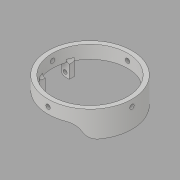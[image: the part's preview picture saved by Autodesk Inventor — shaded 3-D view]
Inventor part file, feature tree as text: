
AUTODESK INVENTOR PART (.ipt)
format: ipt  version: 2017 (Build 210142000, 142)  size: 249,856 bytes
history: native  units: in
note: dims shown in document units (in); Inventor stores cm internally (conversion verified against a paired STEP export)
features: sketch x6, extrude x5, fillet x3, hole x1
ambient origin geometry x8: Origin, YZ Plane, XZ Plane, XY Plane, X Axis, Y Axis, Z Axis, Center Point
bodies: Solid1 (feature_tree)
feature tree (15):
  extrude  "Extrusion1"  Depth=0.2in
  extrude  "Extrusion2"  Depth=1.5in
  hole  "Hole2"  [1 undecoded]
  fillet  "Fillet1"  Radius=0.6in
  extrude  "Extrusion3"  Depth=0.2in
  fillet  "Fillet2"  Radius=0.125in
  fillet  "Fillet3"  Radius=0.6871in
  extrude  "Extrusion4"  Depth=0.3in
  extrude  "Extrusion5"  Depth=0.3in
  sketch  "Sketch1"  dims[d0=3.45in d1=0.2in]
  sketch  "Sketch2"  dims[d2=0.6in d3=0.0in d5=1.5in]
  sketch  "Sketch3"  dims[d6=0.25in d7=1.1in d8=0.6in d9=0.0in]
  sketch  "Sketch4"  dims[d10=0.19in]
  sketch  "Sketch5"  dims[d19=0.18in d20=0.75in d21=0.375in d22=0.25in d23=0.5635in d24=1.0in d25=0.8108in d26=0.2in d27=0.125in d28=0.6871in]
  sketch  "Sketch6"  dims[d29=0.6in d30=0.0in d31=0.625in d32=0.625in d33=0.2in d34=0.3in d35=1.0in d36=0.0in d37=0.2in d38=0.3in d39=1.0in d40=0.0in]
note: 1 required parameter value undecoded (feature->parameter linkage not recoverable at this tier; creation-order binding heuristic only, values carry confidence <= 0.55)
